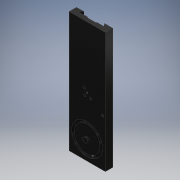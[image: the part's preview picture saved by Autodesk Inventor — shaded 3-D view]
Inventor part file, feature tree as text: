
AUTODESK INVENTOR PART (.ipt)
format: ipt  version: 2018 (Build 220112000, 112)  size: 250,880 bytes
history: native  units: mm
features: extrude x9, sketch x8, hole x4, thread x1, fillet x1
ambient origin geometry x8: Origin, YZ Plane, XZ Plane, XY Plane, X Axis, Y Axis, Z Axis, Center Point
bodies: Solid1 (feature_tree)
feature tree (23):
  extrude  "Extrusion1"  Depth=29.6mm
  sketch  "Sketch2"  dims[d2=29.9mm d4=22.68928mm]
  sketch  "Sketch3"  dims[d5=33.0mm d6=8.726646mm]
  extrude  "Extrusion2"  Depth=29.9mm
  extrude  "Extrusion3"  Depth=33.0mm
  extrude  "Extrusion4"  Depth=486.0mm
  sketch  "Sketch4"  dims[d7=486.0mm d8=0.0mm d9=22.0mm]
  extrude  "Extrusion5"  Depth=14.5mm
  extrude  "Extrusion7"  Depth=62.1mm
  extrude  "Extrusion8"  Depth=8.2mm
  sketch  "Sketch5"  dims[d10=124.2mm d11=14.5mm]
  hole  "Hole1"  [1 undecoded]
  hole  "Hole2"  [1 undecoded]
  hole  "Hole3"  [1 undecoded]
  thread  "Thread1"  [1 undecoded]
  extrude  "Extrusion11"  Depth=9.4mm
  extrude  "Extrusion13"  TaperAngle=0.0deg  [1 undecoded]
  hole  "Hole5"  [1 undecoded]
  fillet  "Fillet1"  Radius=18.7mm
  sketch  "Sketch1"  dims[d0=146.0mm d1=29.6mm]
  sketch  "Sketch14"  dims[d12=62.1mm d13=104.0mm]
  sketch  "Sketch17"  dims[d14=19.02mm d15=8.2mm]
  sketch  "Sketch18"  dims[d17=13.0mm d18=0.0mm d19=7.5mm d20=0.0mm d21=7.5mm d22=0.0mm d23=19.0mm d24=3.7mm d25=0.0mm d26=9.4mm d29=0.0mm d30=18.7mm d31=18.7mm d36=6.0mm d37=0.0mm d38=17.0mm d39=46.5mm d40=3.0mm d41=0.0mm d45=11.0mm d46=60.5mm d47=250.5mm d48=11.0mm d49=190.5mm d50=11.5mm d51=8.5mm d52=6.0mm d53=11.0mm d54=8.5mm d55=90.0deg d56=8.0mm d57=20.594885mm d58=7.0mm d59=0.599mm d60=10.0mm d61=7.5mm d62=90.0deg d63=8.0mm d64=20.594885mm d65=7.5mm d66=6.0mm d67=11.0mm d68=7.0mm d69=90.0deg d70=8.0mm d71=20.594885mm d75=10.0mm d76=0.0mm d82=39.0mm d83=83.1mm d84=64.0mm d85=6.0mm d86=0.0mm d99=19.35mm d100=38.0mm d101=145.0mm d102=3.0mm d103=0.0mm d112=22.7mm d113=7.0mm d114=6.0mm d115=10.0mm d116=7.5mm d117=90.0deg d118=8.0mm d119=20.594885mm d124=10.0mm]
note: 6 required parameter values undecoded (feature->parameter linkage not recoverable at this tier; creation-order binding heuristic only, values carry confidence <= 0.55)
